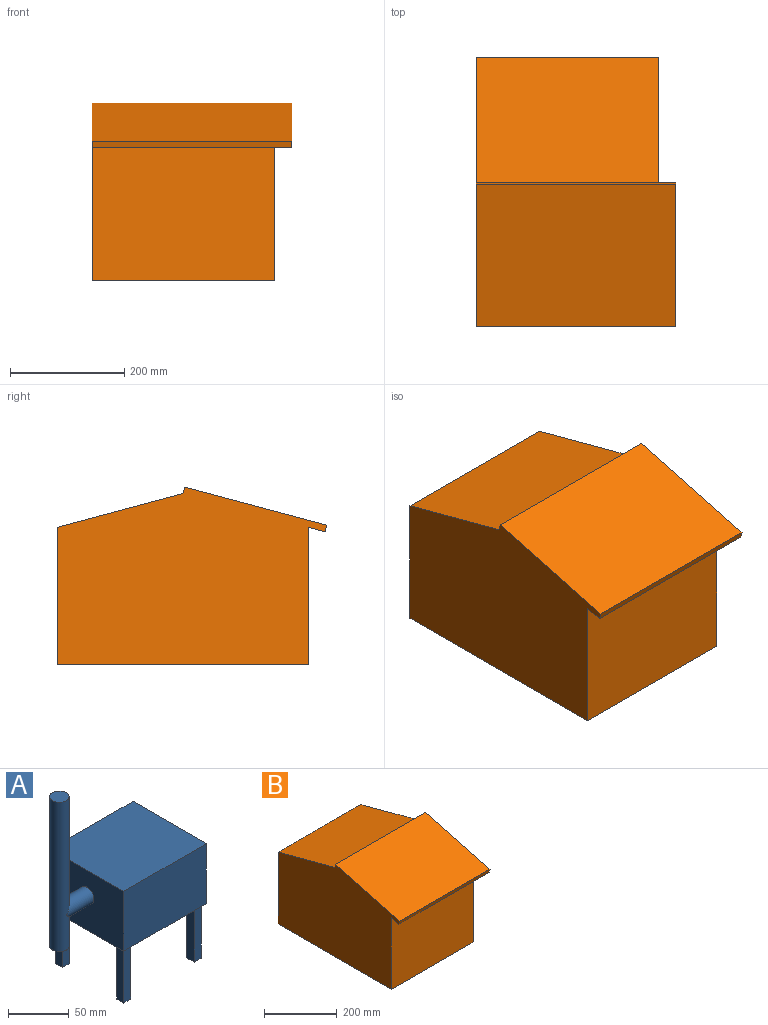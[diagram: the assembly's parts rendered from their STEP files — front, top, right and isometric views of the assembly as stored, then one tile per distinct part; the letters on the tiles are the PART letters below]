
ASSEMBLY  parts=2 mates=1
PART A: 30 faces, bbox 136x85x205 mm
  f0: cylinder r=8mm len=32mm, axis (1,0,0), area 1352.5mm2, adj f2,f27
  f1: plane 96x85mm, normal (0,0,-1), area 7897.8mm2, adj f2,f3,f4,f5,f7,f8,f9,f10
  f2: plane 85x60mm, normal (-1,0,0), area 4898.9mm2, adj f0,f1,f3,f5,f6
  f3: plane 96x60mm, normal (0,-1,0), area 5760mm2, adj f1,f2,f4,f6
  f4: plane 85x60mm, normal (1,0,0), area 5100mm2, adj f1,f3,f5,f6
  f5: plane 96x60mm, normal (0,1,0), area 5760mm2, adj f1,f2,f4,f6
  f6: plane 96x85mm, normal (0,0,1), area 8160mm2, adj f2,f3,f4,f5
  f7: plane 55x8mm, normal (0,1,0), area 440mm2, adj f1,f8,f10,f11
  f8: plane 55x8mm, normal (-1,0,0), area 440mm2, adj f1,f7,f9,f11
  f9: plane 55x8mm, normal (0,-1,0), area 440mm2, adj f1,f8,f10,f11
  f10: plane 55x8mm, normal (1,0,0), area 440mm2, adj f1,f7,f9,f11
  f11: plane 8x8mm, normal (0,0,-1), area 64mm2, adj f7,f8,f9,f10
  f12: plane 55x8mm, normal (0,1,0), area 440mm2, adj f1,f13,f15,f16
  f13: plane 55x8.78mm, normal (-1,0,0), area 482.9mm2, adj f1,f12,f14,f16
  f14: plane 55x8mm, normal (0,-1,0), area 440mm2, adj f1,f13,f15,f16
  f15: plane 55x8.78mm, normal (1,0,0), area 482.9mm2, adj f1,f12,f14,f16
  f16: plane 8.78x8mm, normal (0,0,-1), area 70.2mm2, adj f12,f13,f14,f15
  f17: plane 55x8mm, normal (0,1,0), area 440mm2, adj f1,f18,f20,f21
  f18: plane 55x8mm, normal (-1,0,0), area 440mm2, adj f1,f17,f19,f21
  f19: plane 55x8mm, normal (0,-1,0), area 440mm2, adj f1,f18,f20,f21
  f20: plane 55x8mm, normal (1,0,0), area 440mm2, adj f1,f17,f19,f21
  f21: plane 8x8mm, normal (0,0,-1), area 64mm2, adj f17,f18,f19,f20
  f22: plane 55x8mm, normal (0,1,0), area 440mm2, adj f1,f23,f25,f26
  f23: plane 55x8mm, normal (-1,0,0), area 440mm2, adj f1,f22,f24,f26
  f24: plane 55x8mm, normal (0,-1,0), area 440mm2, adj f1,f23,f25,f26
  f25: plane 55x8mm, normal (1,0,0), area 440mm2, adj f1,f22,f24,f26
  f26: plane 8x8mm, normal (0,0,-1), area 64mm2, adj f22,f23,f24,f25
  f27: cylinder r=8mm len=150mm, axis (0,0,-1), area 7283.8mm2, adj f0,f28,f29
  f28: plane 16x16mm, normal (0,0,1), area 201.1mm2, adj f27
  f29: plane 16x16mm, normal (0,0,-1), area 201.1mm2, adj f27
PART B: 30 faces, bbox 350x472.1x311.6 mm
  f0: plane 440x300mm, normal (1,0,0), area 75031.3mm2, adj f2,f4,f6,f7,f12,f18,f19,f20
  f1: plane 420x299.34mm, normal (-1,0,0), area 68352.5mm2, adj f3,f4,f14,f15,f16,f17,f18,f19
  f2: plane 320x241.05mm, normal (0,1,0), area 72336.4mm2, adj f0,f4,f5,f7,f22,f23,f24,f25
  f3: plane 300x233.38mm, normal (0,-1,0), area 65213.4mm2, adj f1,f4,f13,f15,f22,f23,f24,f25
  f4: plane 440x320mm, normal (0,0,-1), area 14800mm2, adj f0,f1,f2,f3,f5,f6,f13,f14
  f5: plane 472.08x311.59mm, normal (-1,0,0), area 122124.4mm2, adj f2,f4,f6,f7,f8,f10,f11,f12
  f6: plane 320x241.05mm, normal (0,-1,0), area 77136.4mm2, adj f0,f4,f5,f12
  f7: plane 320x220mm, normal (0,0.26,0.97), area 72883.4mm2, adj f0,f2,f5,f10
  f8: plane 350x11.59mm, normal (0,-0.97,-0.26), area 4200mm2, adj f5,f9,f11,f12
  f9: plane 252.08x78.3mm, normal (1,0,0), area 3093.1mm2, adj f8,f10,f11,f12
  f10: plane 350x11.59mm, normal (0,0.97,0.26), area 4200mm2, adj f5,f7,f9,f11,f12
  f11: plane 350x248.98mm, normal (0,-0.26,0.97), area 90216.3mm2, adj f5,f8,f9,f10
  f12: plane 350x248.98mm, normal (0,0.26,-0.97), area 17332.8mm2, adj f0,f5,f6,f8,f9,f10
  f13: plane 420x299.34mm, normal (1,0,0), area 112352.5mm2, adj f3,f4,f14,f15,f16,f17
  f14: plane 300x245.8mm, normal (0,1,0), area 73740.4mm2, adj f1,f4,f13,f17
  f15: plane 300x218.17mm, normal (0,-0.26,-0.97), area 67758.3mm2, adj f1,f3,f13,f16
  f16: plane 300x7.51mm, normal (0,-0.97,-0.26), area 2332.1mm2, adj f1,f13,f15,f17
  f17: plane 300x199.82mm, normal (0,0.26,-0.97), area 62061.6mm2, adj f1,f13,f14,f16
  f18: plane 200x10mm, normal (0,1,0), area 2000mm2, adj f0,f1,f19,f21
  f19: plane 180x10mm, normal (0,0,1), area 1800mm2, adj f0,f1,f18,f20
  f20: plane 200x10mm, normal (0,-1,0), area 2000mm2, adj f0,f1,f19,f21
  f21: plane 180x10mm, normal (0,0,-1), area 1800mm2, adj f0,f1,f18,f20
  f22: plane 60x10mm, normal (-1,0,0), area 600mm2, adj f2,f3,f23,f25
  f23: plane 80x10mm, normal (0,0,1), area 800mm2, adj f2,f3,f22,f24
  f24: plane 60x10mm, normal (1,0,0), area 600mm2, adj f2,f3,f23,f25
  f25: plane 80x10mm, normal (0,0,-1), area 800mm2, adj f2,f3,f22,f24
  f26: plane 100x10mm, normal (0,1,0), area 1000mm2, adj f0,f1,f27,f29
  f27: plane 80x10mm, normal (0,0,1), area 800mm2, adj f0,f1,f26,f28
  f28: plane 100x10mm, normal (0,-1,0), area 1000mm2, adj f0,f1,f27,f29
  f29: plane 80x10mm, normal (0,0,-1), area 800mm2, adj f0,f1,f26,f28
PLACE A rot(axis=(0,0,-1),40deg) t=(-139.67,171.34,-22.68)mm
PLACE B t=(-189.15,54.85,-77.68)mm
MATE planar A.f16 <-> B.f4  axis (0,0,-1) through (-66.74,119.79,-77.68)mm
